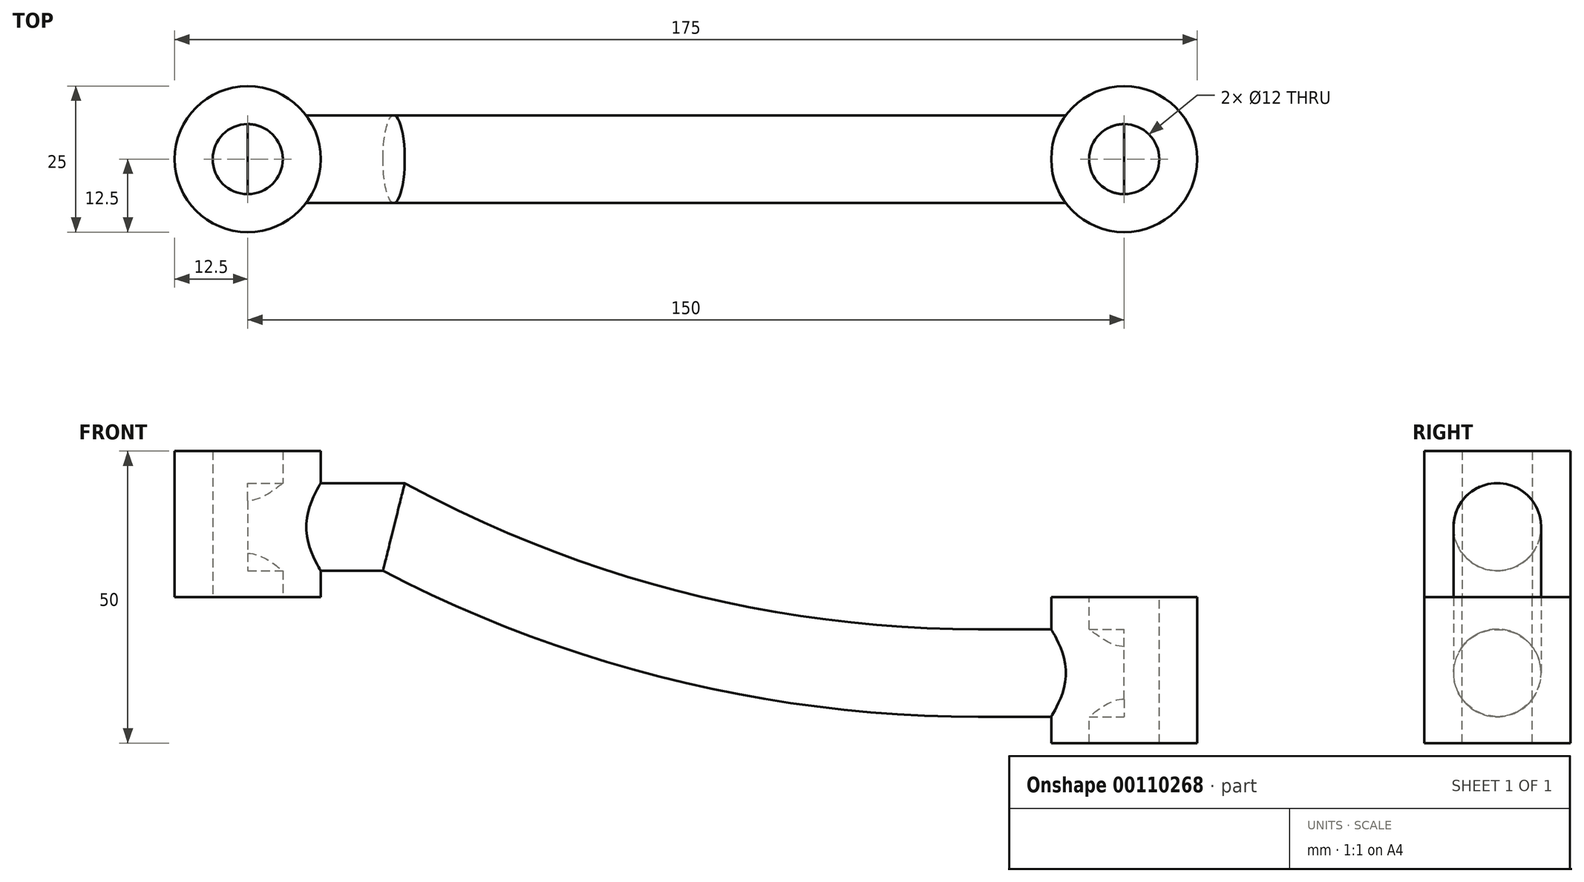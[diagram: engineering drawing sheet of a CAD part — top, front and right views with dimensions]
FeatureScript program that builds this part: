
annotation { "Feature Type Name" : "Feature", "Feature Type Description" : "" }
export const myFeature = defineFeature(function(context is Context, id is Id, definition is map)
    precondition{}
    {
        {
            var Q0;
            Q0=qCreatedBy(makeId("Top.planeOp"),FACE);
            var sketch = newSketch(context, id + "F0", { "sketchPlane" : qUnion([Q0])});
            skCircle(sketch, "E0", {"center": v(0, 0) * mm, "radius": 6 * mm});
            skCircle(sketch, "E1", {"center": v(0, 0) * mm, "radius": 12.5 * mm});
            skCircle(sketch, "E2", {"center": v(150, 0) * mm, "radius": 6 * mm});
            skCircle(sketch, "E3", {"center": v(150, 0) * mm, "radius": 12.5 * mm});
            skSolve(sketch);
        }
        {
            var Q0;
            Q0=makeQuery(id+"F0.imprint","IMPRINT",FACE,{"disambiguationData":[TD([[makeQuery(id+"F0.imprint","IMPRINT",EDGE,{"derivedFrom":sQuery(id+"F0.wireOp",EDGE,"E0")}),-1.0]])]});
            extrude(context, id + "F1", {"entities" : qUnion([Q0]), "depth" : 25 * mm});
        }
        {
            var Q0;
            Q0=makeQuery(id+"F0.imprint","IMPRINT",FACE,{"disambiguationData":[TD([[makeQuery(id+"F0.imprint","IMPRINT",EDGE,{"derivedFrom":sQuery(id+"F0.wireOp",EDGE,"E2")}),-1.0]])]});
            extrude(context, id + "F2", {"entities" : qUnion([Q0]), "oppositeDirection" : true, "depth" : 25 * mm});
        }
        {
            var Q0;
            Q0=qCreatedBy(makeId("Front.planeOp"),FACE);
            var sketch = newSketch(context, id + "F3", { "sketchPlane" : qUnion([Q0])});
            skLineSegment(sketch, "E4", {"start": v(0, 12) * mm, "end": v(25, 12) * mm});
            skLineSegment(sketch, "E5", {"start": v(150, -13) * mm, "end": v(125, -13) * mm});
            skArc(sketch, "E6", {"start": v(125, -13) * mm, "mid": v(73.46, -6.66) * mm, "end": v(25, 12) * mm});
            skSolve(sketch);
        }
        {
            var Q0;
            Q0=qCreatedBy(makeId("Right.planeOp"),FACE);
            var sketch = newSketch(context, id + "F4", { "sketchPlane" : qUnion([Q0])});
            skCircle(sketch, "E7", {"center": v(0, 12) * mm, "radius": 7.5 * mm});
            skSolve(sketch);
        }
        {
            var Q0;
            Q0 = qSketchRegion(id + "F4", true);
            var Q1;
            Q1 = qConstructionFilter(qBodyType(qCreatedBy(id + "F3" ,EDGE), BodyType.WIRE), ConstructionObject.NO);
            sweep(context, id + "F5", {"operationType" : NewBodyOperationType.ADD, "profiles" : qUnion([Q0]), "path" : qUnion([Q1])});
        }
    });
